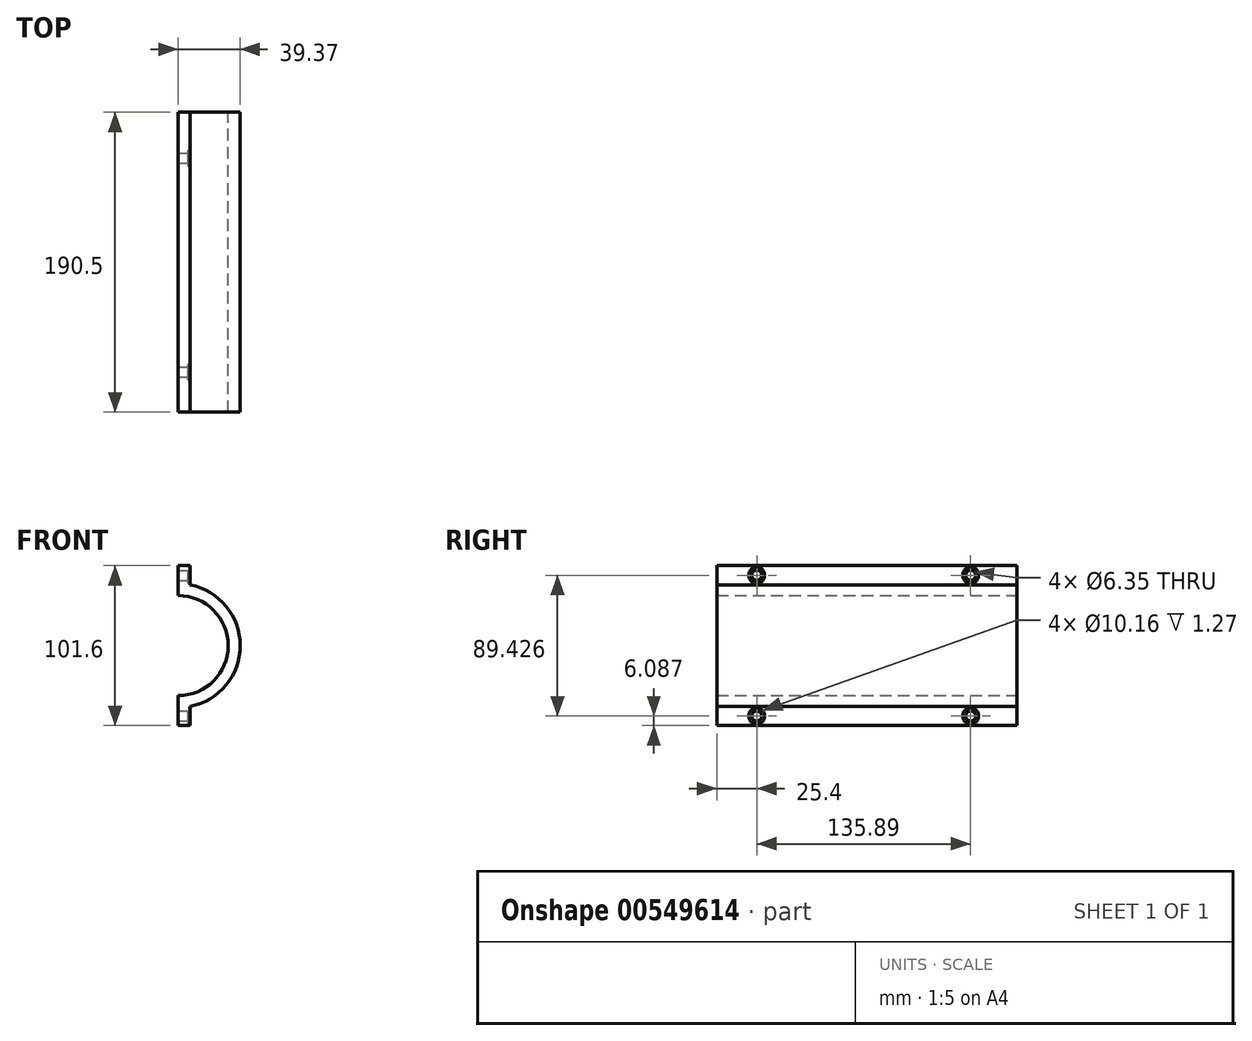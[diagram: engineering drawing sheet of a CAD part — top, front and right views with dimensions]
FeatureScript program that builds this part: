
annotation { "Feature Type Name" : "Feature", "Feature Type Description" : "" }
export const myFeature = defineFeature(function(context is Context, id is Id, definition is map)
    precondition{}
    {
        {
            var Q0;
            Q0=qCreatedBy(makeId("Front.planeOp"),FACE);
            var sketch = newSketch(context, id + "F0", { "sketchPlane" : qUnion([Q0])});
            skLineSegment(sketch, "E0", {"start": v(0, 31.75) * mm, "end": v(0, 50.8) * mm});
            skLineSegment(sketch, "E1", {"start": v(0, 50.8) * mm, "end": v(7.62, 50.8) * mm});
            skLineSegment(sketch, "E2", {"start": v(7.62, 50.8) * mm, "end": v(7.62, 38.63) * mm});
            skArc(sketch, "E3", {"start": v(7.62, -38.63) * mm, "mid": v(39.37, 0) * mm, "end": v(7.62, 38.63) * mm});
            skArc(sketch, "E4", {"start": v(0, -31.75) * mm, "mid": v(31.75, 0) * mm, "end": v(0, 31.75) * mm});
            skLineSegment(sketch, "E5", {"start": v(0, -31.75) * mm, "end": v(0, -50.8) * mm});
            skLineSegment(sketch, "E6", {"start": v(0, -50.8) * mm, "end": v(7.62, -50.8) * mm});
            skLineSegment(sketch, "E7", {"start": v(7.62, -50.8) * mm, "end": v(7.62, -38.63) * mm});
            skSolve(sketch);
        }
        {
            var Q0;
            Q0 = qSketchRegion(id + "F0", true);
            extrude(context, id + "F1", {"entities" : qUnion([Q0]), "depth" : 190.5 * mm, "offsetDistance" : 25.4 * mm});
        }
        {
            var Q0;
            Q0=makeQuery(id+"F1.opExtrude","SWEPT_FACE",FACE,{"disambiguationData":[OSD([sQuery(id+"F0.wireOp",EDGE,"E2")])]});
            var sketch = newSketch(context, id + "F2", { "sketchPlane" : qUnion([Q0])});
            skCircle(sketch, "E8", {"center": v(-165.1, 44.71) * mm, "radius": 3.81 * mm});
            skCircle(sketch, "E9", {"center": v(-29.21, 44.71) * mm, "radius": 3.81 * mm});
            skCircle(sketch, "E10", {"center": v(-165.1, -44.71) * mm, "radius": 3.81 * mm});
            skCircle(sketch, "E11", {"center": v(-29.2, -44.71) * mm, "radius": 3.81 * mm});
            skSolve(sketch);
        }
        {
            var Q0;
            Q0=sQuery(id+"F2.wireOp",VERTEX,"E10.center");
            var Q1;
            Q1=sQuery(id+"F2.wireOp",VERTEX,"E11.center");
            var Q2;
            Q2=sQuery(id+"F2.wireOp",VERTEX,"E9.center");
            var Q3;
            Q3=sQuery(id+"F2.wireOp",VERTEX,"E8.center");
            var Q4;
            Q4=makeQuery(id+"F1.opExtrude","SWEPT_BODY",BODY,{"disambiguationData":[OSD([sQuery(id+"F0.wireOp",EDGE,"E0"),sQuery(id+"F0.wireOp",EDGE,"E1"),sQuery(id+"F0.wireOp",EDGE,"E2"),sQuery(id+"F0.wireOp",EDGE,"E3"),sQuery(id+"F0.wireOp",EDGE,"E4"),sQuery(id+"F0.wireOp",EDGE,"E5"),sQuery(id+"F0.wireOp",EDGE,"E6"),sQuery(id+"F0.wireOp",EDGE,"E7")])]});
            hole(context, id + "F3", {"style" : HoleStyle.C_BORE, "endStyle" : HoleEndStyle.THROUGH, "holeDiameter" : 6.35 * mm, "cBoreDiameter" : 10.16 * mm, "cBoreDepth" : 1.27 * mm, "isTappedThrough" : true, "tappedDepth" : 12.7 * mm, "tapClearance" : 3, "locations" : qUnion([Q0, Q1, Q2, Q3]), "scope" : qUnion([Q4])});
        }
    });
